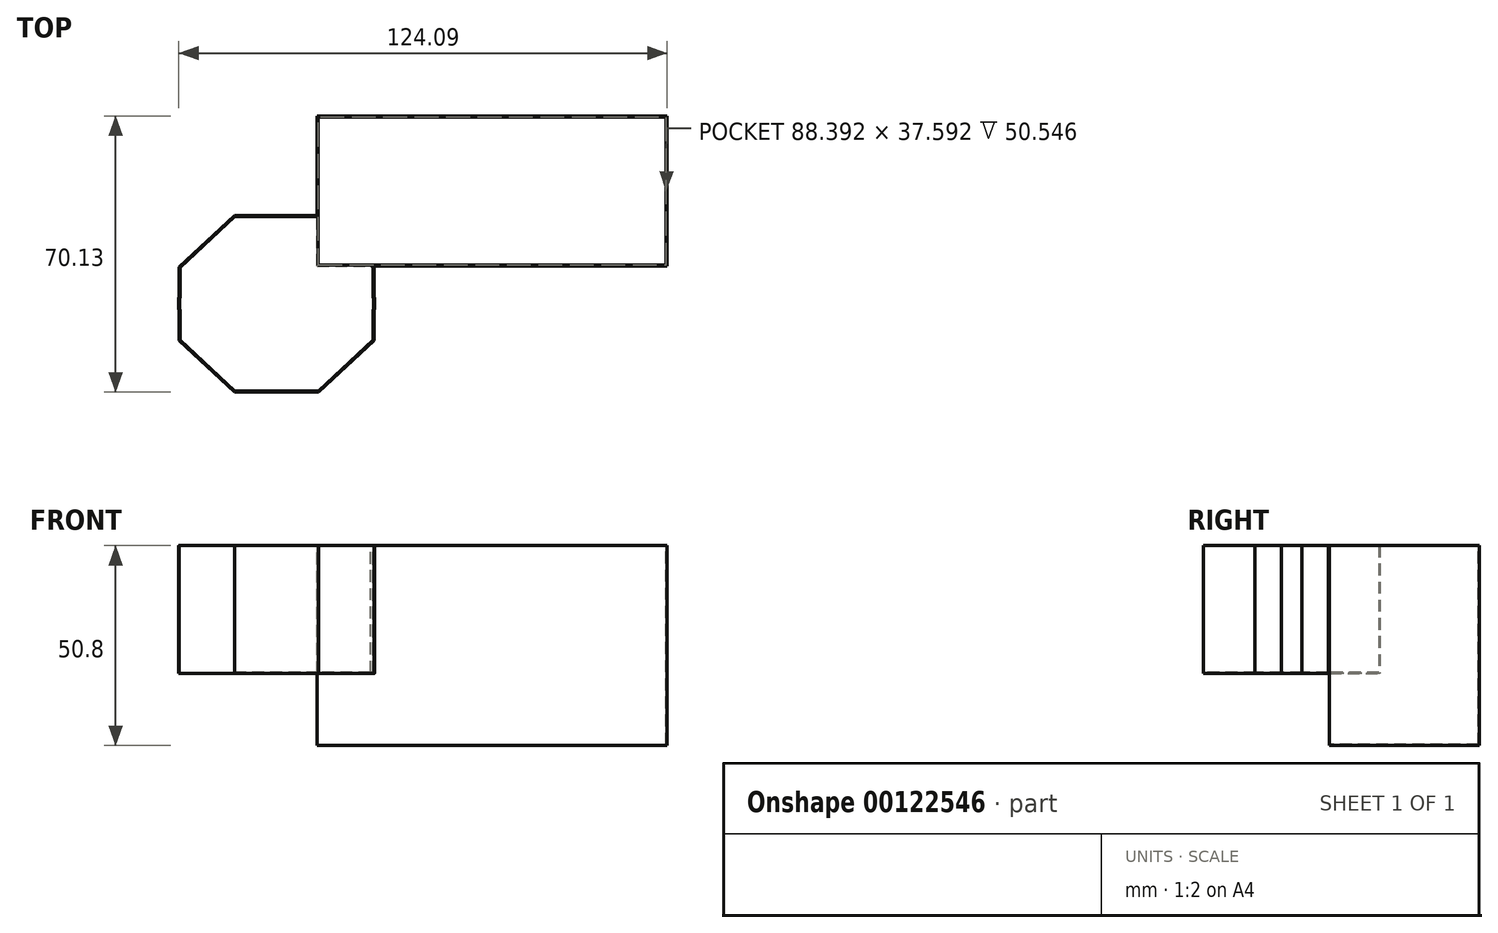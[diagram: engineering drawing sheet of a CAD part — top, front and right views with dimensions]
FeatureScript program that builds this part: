
annotation { "Feature Type Name" : "Feature", "Feature Type Description" : "" }
export const myFeature = defineFeature(function(context is Context, id is Id, definition is map)
    precondition{}
    {
        {
            var Q0;
            Q0=qCreatedBy(makeId("Top.planeOp"),FACE);
            var sketch = newSketch(context, id + "F0", { "sketchPlane" : qUnion([Q0])});
            skArc(sketch, "E0", {"start": v(-129.09, 2.63) * mm, "mid": v(-129.23, 0) * mm, "end": v(-129.09, -2.63) * mm});
            skLineSegment(sketch, "E1.bottom", {"start": v(-93.63, -22.44) * mm, "end": v(-115.08, -22.44) * mm});
            skLineSegment(sketch, "E1.top", {"start": v(-93.63, 22.44) * mm, "end": v(-115.08, 22.44) * mm});
            skLineSegment(sketch, "E2.left", {"start": v(-79.62, 9.33) * mm, "end": v(-79.62, -9.33) * mm});
            skLineSegment(sketch, "E2.right", {"start": v(-129.09, 9.33) * mm, "end": v(-129.09, -9.33) * mm});
            skArc(sketch, "E3.trimOffspring", {"start": v(-79.62, -2.63) * mm, "mid": v(-79.48, 0) * mm, "end": v(-79.62, 2.63) * mm});
            skLineSegment(sketch, "E4", {"start": v(-93.63, -22.44) * mm, "end": v(-79.62, -9.33) * mm});
            skLineSegment(sketch, "E5", {"start": v(-79.62, 9.33) * mm, "end": v(-93.63, 22.44) * mm});
            skLineSegment(sketch, "E6", {"start": v(-115.08, 22.44) * mm, "end": v(-129.09, 9.33) * mm});
            skLineSegment(sketch, "E7", {"start": v(-129.09, -9.33) * mm, "end": v(-115.08, -22.44) * mm});
            skPoint(sketch, "E8.orphan", {"position": v(-93.63, 47.35) * mm});
            skSolve(sketch);
        }
        {
            var Q0;
            Q0=qCreatedBy(makeId("Top.planeOp"),FACE);
            var sketch = newSketch(context, id + "F1", { "sketchPlane" : qUnion([Q0])});
            skLineSegment(sketch, "E9.bottom", {"start": v(-94.04, 47.7) * mm, "end": v(-5.14, 47.7) * mm});
            skLineSegment(sketch, "E9.top", {"start": v(-94.04, 9.6) * mm, "end": v(-5.14, 9.6) * mm});
            skLineSegment(sketch, "E9.left", {"start": v(-94.04, 47.7) * mm, "end": v(-94.04, 9.6) * mm});
            skLineSegment(sketch, "E9.right", {"start": v(-5.14, 47.7) * mm, "end": v(-5.14, 9.6) * mm});
            skSolve(sketch);
        }
        {
            var Q0;
            Q0 = qSketchRegion(id + "F1", true);
            extrude(context, id + "F2", {"entities" : qUnion([Q0]), "oppositeDirection" : true, "depth" : 50.8 * mm});
        }
        {
            var Q0;
            Q0 = qSketchRegion(id + "F0", true);
            extrude(context, id + "F3", {"entities" : qUnion([Q0]), "operationType" : NewBodyOperationType.ADD, "oppositeDirection" : true, "depth" : 32.5 * mm});
        }
        {
            var Q0;
            Q0=makeQuery(id+"F3.boolean.opBoolean","MERGE",FACE,{"derivedFrom":[makeQuery(id+"F2.opExtrude","CAP_FACE",FACE,{"disambiguationData":[OSD([sQuery(id+"F1.wireOp",EDGE,"E9.bottom"),sQuery(id+"F1.wireOp",EDGE,"E9.top"),sQuery(id+"F1.wireOp",EDGE,"E9.left"),sQuery(id+"F1.wireOp",EDGE,"E9.right")])],"isStart":true}),makeQuery(id+"F3.opExtrude","CAP_FACE",FACE,{"disambiguationData":[OSD([sQuery(id+"F0.wireOp",EDGE,"E0"),sQuery(id+"F0.wireOp",EDGE,"E1.bottom"),sQuery(id+"F0.wireOp",EDGE,"E1.top"),sQuery(id+"F0.wireOp",EDGE,"E2.left"),sQuery(id+"F0.wireOp",EDGE,"E2.right"),sQuery(id+"F0.wireOp",EDGE,"E3.trimOffspring"),sQuery(id+"F0.wireOp",EDGE,"E4"),sQuery(id+"F0.wireOp",EDGE,"E5"),sQuery(id+"F0.wireOp",EDGE,"E6"),sQuery(id+"F0.wireOp",EDGE,"E7")])],"isStart":true})]});
            shell(context, id + "F4", {"entities" : qUnion([Q0]), "thickness" : 0.25 * mm});
        }
    });
